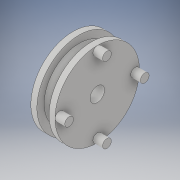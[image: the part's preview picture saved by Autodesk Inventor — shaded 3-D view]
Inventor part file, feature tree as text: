
AUTODESK INVENTOR PART (.ipt)
format: ipt  version: 2019 (Build 230136000, 136)  size: 145,408 bytes
history: native  units: in
note: dims shown in document units (in); Inventor stores cm internally (conversion verified against a paired STEP export)
features: sketch x3, revolve x1, extrude x1
ambient origin geometry x8: Origin, YZ Plane, XZ Plane, XY Plane, X Axis, Y Axis, Z Axis, Center Point
bodies: Body1 (feature_tree)
feature tree (5):
  sketch  "Sketch3"  dims[d10=0.685in d11=0.3937in]
  sketch  "Sketch4"  dims[d12=0.0984in d13=0.1181in]
  revolve  "Revolution1"  [1 undecoded]
  extrude  "Extrusion3"  Depth=0.1181in
  sketch  "Sketch5"  dims[d14=0.1969in d15=90.0deg d16=0.1417in d17=0.1417in d18=0.1417in d19=0.1417in d22=0.1575in d23=0.0in d24=0.2362in d25=0.5669in]
note: 1 required parameter value undecoded (feature->parameter linkage not recoverable at this tier; creation-order binding heuristic only, values carry confidence <= 0.55)
